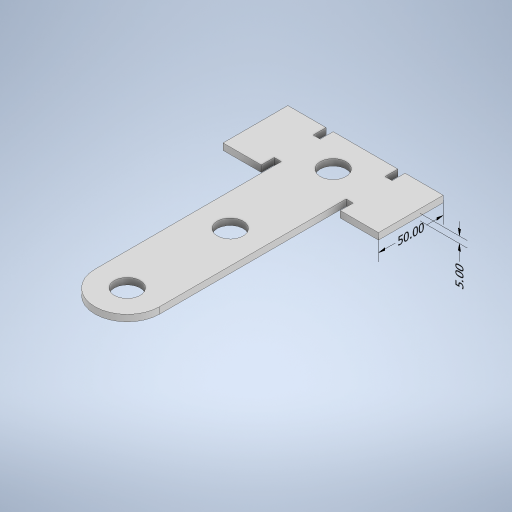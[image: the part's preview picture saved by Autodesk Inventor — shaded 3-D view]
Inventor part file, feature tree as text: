
AUTODESK INVENTOR PART (.ipt)
format: ipt  version: 2024.1 (Build 281209000, 209)  size: 305,152 bytes
history: native  units: mm
features: other x3, extrude x3, sketch x3, projected_geometry x1
ambient origin geometry x8: Origin, YZ Plane, XZ Plane, XY Plane, X Axis, Y Axis, Z Axis, Center Point
bodies: Body1 (feature_tree)
feature tree (10):
  other  "ソリッド1"
  extrude  "押し出し1"  Depth=114.0mm
  extrude  "押し出し2"  Depth=45.0mm
  extrude  "押し出し3"  Depth=150.0mm
  sketch  "スケッチ1"
  sketch  "スケッチ2"
  projected_geometry  "投影ループ1"
  sketch  "スケッチ3"
  other  "長さ寸法 1"
  other  "長さ寸法 2"
